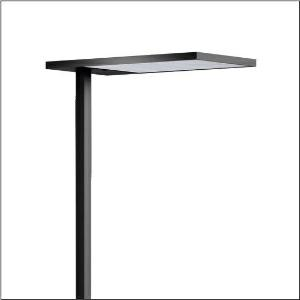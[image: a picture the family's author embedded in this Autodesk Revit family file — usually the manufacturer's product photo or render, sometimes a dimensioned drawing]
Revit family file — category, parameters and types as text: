
# Revit family: silica_21_floor_r_51mx53sg4db
name_source: partatom
category: Lighting Fixtures
units: mm (PartAtom-declared; Revit-internal decimal feet)

## family parameters
Cut with Voids When Loaded = No
Host = Face
Light Source = No
Part Type = Normal
Room Calculation Point = No
Round Connector Dimension = Use Diameter
Shared = No

## types (1)
- Silica 21 Floor R (1 x LED, 15000 lm, 106.4 W, 4000K)
    Apparent Load = 106 VA
    CIE Flux Codes = 54 86 97 13 100
    Color Rendering = 80
    Color Temperature = 4000K
    Default Elevation = 1800 mm
    Description = Silica® 21 Floor R, floorstanding luminaire, of PMMA, primary optical cover: prismatic diffuser, of PMMA, CAT 2 (L<= 3000cd/m²), light emission: indirect/direct distribution, primary light characteristic: symmetric, primary optical cover: cover panel, of PMMA, installation type: not mounted, LED, rated luminous flux: 15.000lm, luminous efficacy: 141lm/W, light colour: 840, colour temperature: 4000K, control gear: DALI 2, daylight-dependent control, mains connection: 230V, AC, 50/60Hz, connection cable included, cable length: 2,5m, rated input power: 106.4W, luminaire head, of aluminium, powder-coated, jet black (RAL 9005), length: 671mm, width: 371mm, height: 2010mm, supporting column, angular, of aluminium, powder-coated, jet black (RAL 9005), baseplate, of steel, powder-coated, jet black (RAL 9005), sensor module PR3-S, local control - self-sufficient standalone sensors, equipment: master, dimmable, protection rating (complete): IP20, insulation class (complete): insulation class I (protective earthing), certification: CE, permissible operating ambient temperature: 0..+35°C, standard: EN 50419, packaging unit: 1 piece
    Height = 18 mm
    Lamp = 1 x LED
    Lamp Light Flux = 15000 lm
    Lamp Power = 106.4 W
    Lamp count = 1
    Length = 650 mm
    Luminous efficacy = 141 lm/W
    Manufacturer = Siteco
    ModVariant = No
    Model = 51MX53SG4DB
    Mounting Place = Floor
    Mounting Type = Freestanding
    Number of Poles = 1
    OnlyDefault = Yes
    Power Factor = 1
    Product Name = Silica 21 Floor R
    Product group = floorstanding luminaire
    ProductGroupID = 1302
    Protection Class = Protection class I
    Protection Degree = IP 20
    RLX_Detail_Level = 1
    RLX_Emergency_Light_Flux = 0 lm
    RLX_Emergency_Type = 0
    RLX_Emergency_Type_DB = No
    RlxData = <blob elided: 22313 chars, md5=24db1fba>
    Socket = socket
    Standby Power = 0 W
    System Light Flux = 15000 lm
    System Power = 106 W
    Type Comments = Product without accessories
    Type Image = l_1007011.jpg
    URL = http://relux.com
    VarID = ---
    Voltage = 0 V
    Weight = 0.00 kg
    Width = 350 mm

## geometry (parser evidence)
native form markers: Blend x4, Sweep x14
no freeform markers — native parametric forms only
